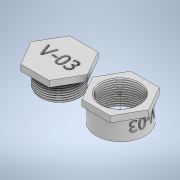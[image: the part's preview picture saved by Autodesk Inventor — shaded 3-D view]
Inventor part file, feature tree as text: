
AUTODESK INVENTOR PART (.ipt)
format: ipt  version: 2021.1 (Build 251245000, 245)  size: 954,368 bytes
history: native  units: in
note: dims shown in document units (in); Inventor stores cm internally (conversion verified against a paired STEP export)
features: sketch x9, extrude x6, helix x2, plane x1, other x1
ambient origin geometry x8: Origin, YZ Plane, XZ Plane, XY Plane, X Axis, Y Axis, Z Axis, Center Point
bodies: Body1 (feature_tree)
feature tree (19):
  extrude  "NutShaft"  Depth=1.0in
  helix  "CoilForNut"  [1 undecoded]
  extrude  "BoltHexHead"  Depth=0.0045in
  extrude  "BoltShaft"  Depth=0.0833in
  helix  "CoilForBolt"  [1 undecoded]
  extrude  "EmbossForBolt"  Depth=2.5in
  plane  "Work Plane4"
  other  "EmbossForNut"
  extrude  "NutHexHead"  Depth=0.25in
  extrude  "HoleForBolt"  Depth=0.75in TaperAngle=0.0deg
  sketch  "Sketch4"  dims[d4=2.0in d5=1.5528in d6=1.0in d7=0.0in]
  sketch  "Sketch6"  dims[d33=60.0deg d35=0.0045in]
  sketch  "Sketch7"  dims[d36=0.8224in d37=0.0833in d38=0.0833in]
  sketch  "Sketch8"  dims[d39=1.1667in d40=0.3937in d41=0.0in d42=90.0deg d43=90.0deg d44=0.0in d45=0.0in d46=2.5in]
  sketch  "Sketch9"  dims[d47=0.25in d48=0.0in d49=1.6118in]
  sketch  "Sketch11"  dims[d50=2.0in d51=0.75in d52=0.0in]
  sketch  "Sketch12"  dims[d53=60.0deg]
  sketch  "Sketch13"  dims[d54=0.0074in]
  sketch  "Sketch14"  dims[d56=0.8059in d57=0.7518in d58=0.0833in d59=0.8333in d60=0.3937in d61=0.0in d62=90.0deg d63=90.0deg d64=0.0in d65=0.0in d66=0.0833in d68=0.1in d69=0.0in d70=1.0in d71=0.1in d72=0.0in d73=2.0in d74=0.25in d75=0.0in d76=0.75in d77=0.0in d78=0.7764in]
note: 2 required parameter values undecoded (feature->parameter linkage not recoverable at this tier; creation-order binding heuristic only, values carry confidence <= 0.55)
